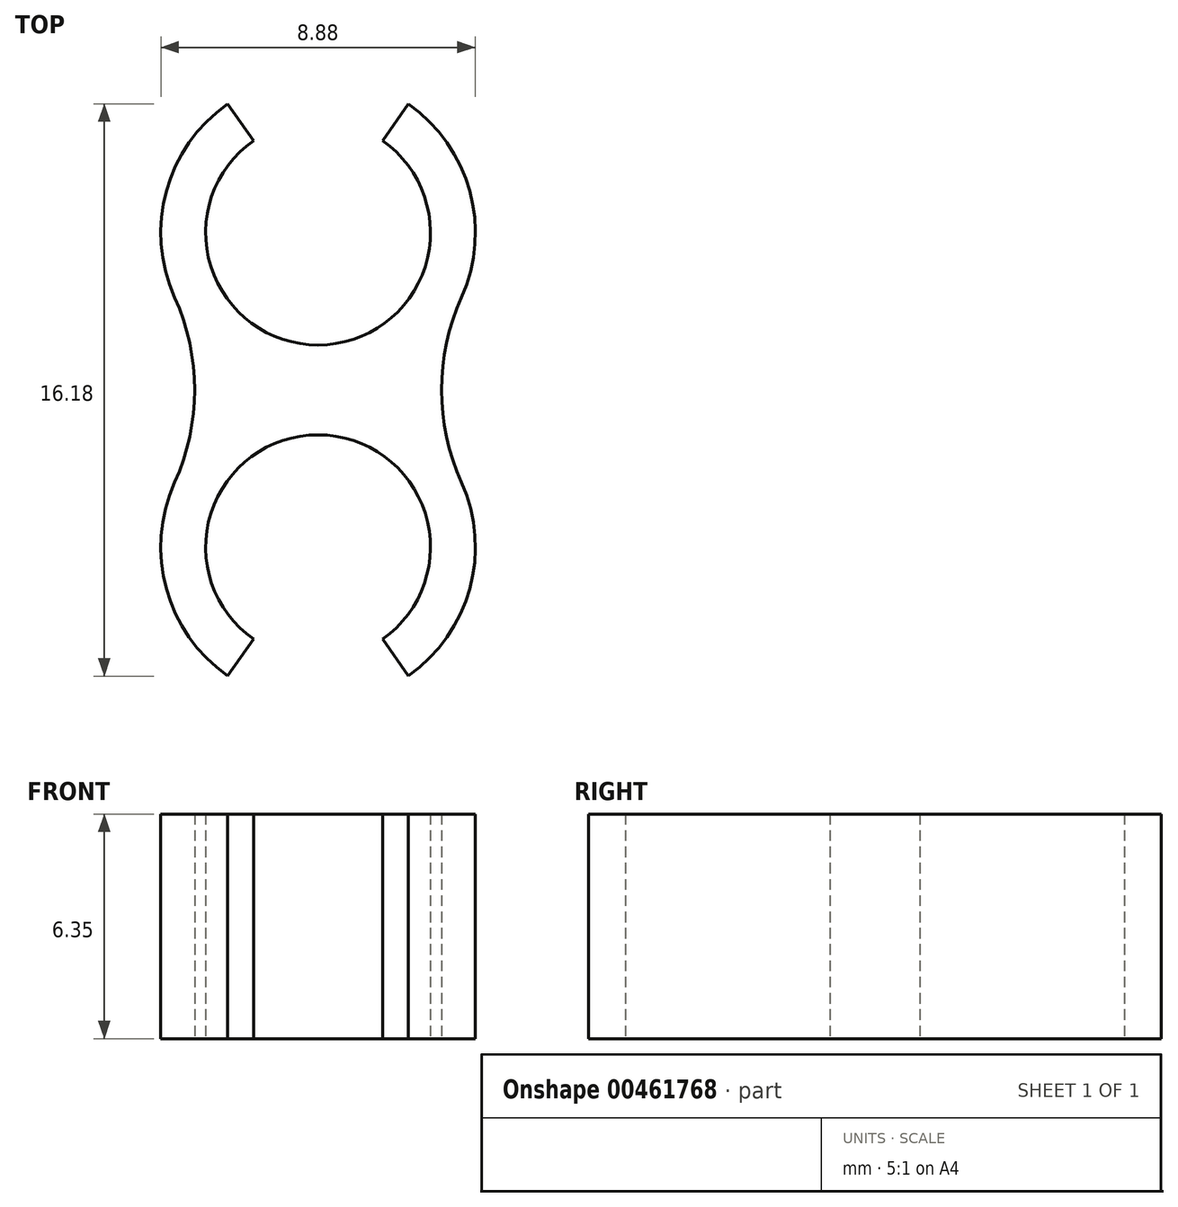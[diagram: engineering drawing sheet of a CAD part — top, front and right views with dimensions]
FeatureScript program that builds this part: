
annotation { "Feature Type Name" : "Feature", "Feature Type Description" : "" }
export const myFeature = defineFeature(function(context is Context, id is Id, definition is map)
    precondition{}
    {
        {
            var Q0;
            Q0=qCreatedBy(makeId("Top.planeOp"),FACE);
            var sketch = newSketch(context, id + "F0", { "sketchPlane" : qUnion([Q0])});
            skArc(sketch, "E0", {"start": v(-1.82, 7.05) * mm, "mid": v(0, 1.27) * mm, "end": v(1.82, 7.05) * mm});
            skArc(sketch, "E1", {"start": v(-2.55, 8.09) * mm, "mid": v(-4.29, 5.62) * mm, "end": v(-4.05, 2.61) * mm});
            skLineSegment(sketch, "E2", {"start": v(-2.55, 8.09) * mm, "end": v(-1.82, 7.05) * mm});
            skLineSegment(sketch, "E3", {"start": v(2.55, 8.09) * mm, "end": v(1.82, 7.05) * mm});
            skArc(sketch, "E4.MirrorCS", {"start": v(-2.55, -8.09) * mm, "mid": v(-4.29, -5.62) * mm, "end": v(-4.05, -2.61) * mm});
            skArc(sketch, "E5.MirrorCS", {"start": v(-1.82, -7.05) * mm, "mid": v(0, -1.27) * mm, "end": v(1.82, -7.05) * mm});
            skLineSegment(sketch, "E6.MirrorCS", {"start": v(2.55, -8.09) * mm, "end": v(1.82, -7.05) * mm});
            skLineSegment(sketch, "E7.MirrorCS", {"start": v(-2.55, -8.09) * mm, "end": v(-1.82, -7.05) * mm});
            skPoint(sketch, "E8.newPointA", {"position": v(2.55, 8.09) * mm});
            skPoint(sketch, "E8.newPointB", {"position": v(2.55, -8.09) * mm});
            skArc(sketch, "E8.filletArc", {"start": v(-4.05, -2.61) * mm, "mid": v(-3.49, 0) * mm, "end": v(-4.05, 2.61) * mm});
            skArc(sketch, "E9.MirrorCS", {"start": v(2.55, 8.09) * mm, "mid": v(4.29, 5.62) * mm, "end": v(4.05, 2.61) * mm});
            skArc(sketch, "E10.MirrorCS", {"start": v(4.05, -2.61) * mm, "mid": v(3.49, 0) * mm, "end": v(4.05, 2.61) * mm});
            skArc(sketch, "E11.MirrorCS", {"start": v(2.55, -8.09) * mm, "mid": v(4.29, -5.62) * mm, "end": v(4.05, -2.61) * mm});
            skSolve(sketch);
        }
        {
            var Q0;
            Q0=makeQuery(id+"F0.imprint","IMPRINT",FACE,{"disambiguationData":[TD([[makeQuery(id+"F0.imprint","IMPRINT",EDGE,{"derivedFrom":sQuery(id+"F0.wireOp",EDGE,"E0")}),-1.0]])]});
            extrude(context, id + "F1", {"entities" : qUnion([Q0]), "depth" : 6.35 * mm});
        }
    });
